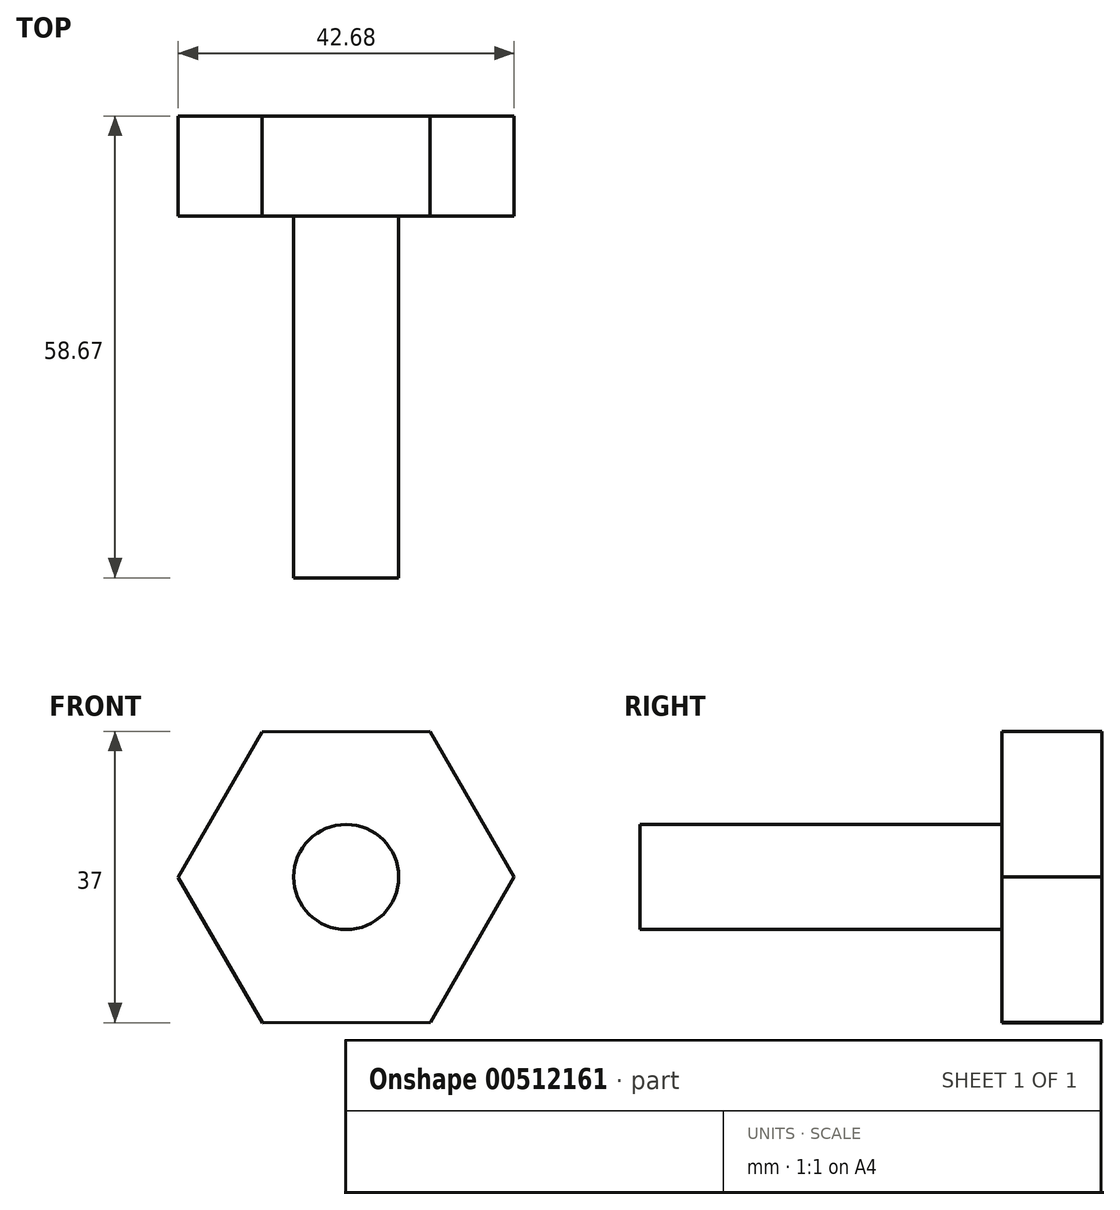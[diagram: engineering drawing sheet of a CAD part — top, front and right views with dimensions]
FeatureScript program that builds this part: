
annotation { "Feature Type Name" : "Feature", "Feature Type Description" : "" }
export const myFeature = defineFeature(function(context is Context, id is Id, definition is map)
    precondition{}
    {
        {
            var Q0;
            Q0=qCreatedBy(makeId("Front.planeOp"),FACE);
            var sketch = newSketch(context, id + "F0", { "sketchPlane" : qUnion([Q0])});
            skCircle(sketch, "E0.cCircle", {"center": v(0, 0) * mm, "radius": 18.48 * mm, "construction": true});
            skLineSegment(sketch, "E0.0", {"start": v(-21.34, -0.05) * mm, "end": v(-10.71, 18.45) * mm});
            skLineSegment(sketch, "E0.1", {"start": v(-10.71, 18.45) * mm, "end": v(10.63, 18.5) * mm});
            skLineSegment(sketch, "E0.2", {"start": v(10.63, 18.5) * mm, "end": v(21.34, 0.05) * mm});
            skLineSegment(sketch, "E0.3", {"start": v(21.34, 0.05) * mm, "end": v(10.71, -18.45) * mm});
            skLineSegment(sketch, "E0.4", {"start": v(10.71, -18.45) * mm, "end": v(-10.63, -18.5) * mm});
            skLineSegment(sketch, "E0.5", {"start": v(-10.63, -18.5) * mm, "end": v(-21.34, -0.05) * mm});
            skPoint(sketch, "E0.0.midPoint", {"position": v(-16.02, 9.2) * mm});
            skSolve(sketch);
        }
        {
            var Q0;
            Q0=makeQuery(id+"F0.imprint","IMPRINT",FACE,{"disambiguationData":[TD([[makeQuery(id+"F0.imprint","IMPRINT",EDGE,{"derivedFrom":sQuery(id+"F0.wireOp",EDGE,"E0.0")}),-1.0]])]});
            extrude(context, id + "F1", {"entities" : qUnion([Q0]), "oppositeDirection" : true, "depth" : 12.7 * mm});
        }
        {
            var Q0;
            Q0=makeQuery(id+"F1.opExtrude","CAP_FACE",FACE,{"disambiguationData":[OSD([sQuery(id+"F0.wireOp",EDGE,"E0.0"),sQuery(id+"F0.wireOp",EDGE,"E0.1"),sQuery(id+"F0.wireOp",EDGE,"E0.2"),sQuery(id+"F0.wireOp",EDGE,"E0.3"),sQuery(id+"F0.wireOp",EDGE,"E0.4"),sQuery(id+"F0.wireOp",EDGE,"E0.5")])],"isStart":true});
            var sketch = newSketch(context, id + "F2", { "sketchPlane" : qUnion([Q0])});
            skCircle(sketch, "E1", {"center": v(0, 0) * mm, "radius": 6.67 * mm});
            skSolve(sketch);
        }
        {
            var Q0;
            Q0=makeQuery(id+"F2.imprint","IMPRINT",FACE,{"disambiguationData":[TD([[makeQuery(id+"F2.imprint","IMPRINT",EDGE,{"derivedFrom":sQuery(id+"F2.wireOp",EDGE,"E1")}),1.0]])]});
            extrude(context, id + "F3", {"entities" : qUnion([Q0]), "operationType" : NewBodyOperationType.ADD, "depth" : 45.97 * mm});
        }
    });
